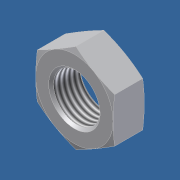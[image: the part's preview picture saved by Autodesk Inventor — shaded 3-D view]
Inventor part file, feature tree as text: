
AUTODESK INVENTOR PART (.ipt)
format: ipt  version: unknown  size: 219,648 bytes
history: native  units: in
note: dims shown in document units (in); Inventor stores cm internally (conversion verified against a paired STEP export)
features: other x70, sketch x3, revolve x2, extrude x1, thread x1
ambient origin geometry x8: Origin, YZ Plane, XZ Plane, XY Plane, X Axis, Y Axis, Z Axis, Center Point
feature tree (77):
  sketch  "Sketch_8"  dims[d0=360.0deg d1=0.38in d2=0.0in]
  sketch  "Sketch_10"  dims[d3=360.0deg d4=0.38in d5=0.0in]
  revolve  "Revolution1"  [1 undecoded]
  extrude  "Extrusion1"  Depth=0.38in TaperAngle=0.0deg
  revolve  "Revolution2"  [1 undecoded]
  thread  "Thread1"  [1 undecoded]
  other  "NUT_XY"
  other  "NUT_YZ"
  other  "NUT_ZX"
  other  "NUT_X"
  other  "NUT_Y"
  other  "NUT_Z"
  other  "NUT_Center"
  other  "a1_XY"
  other  "a1_YZ"
  other  "a1_ZX"
  other  "a1_X"
  other  "a1_Y"
  other  "a1_Z"
  other  "a1_Center"
  other  "a2_XY"
  other  "a2_YZ"
  other  "a2_ZX"
  other  "a2_X"
  other  "a2_Y"
  other  "a2_Z"
  other  "a2_Center"
  other  "b1_XY"
  other  "b1_YZ"
  other  "b1_ZX"
  other  "b1_X"
  other  "b1_Y"
  other  "b1_Z"
  other  "b1_Center"
  other  "b2_XY"
  other  "b2_YZ"
  other  "b2_ZX"
  other  "b2_X"
  other  "b2_Y"
  other  "b2_Z"
  other  "b2_Center"
  other  "e_XY"
  other  "e_YZ"
  other  "e_ZX"
  other  "e_X"
  other  "e_Y"
  other  "e_Z"
  other  "e_Center"
  other  "th1_XY"
  other  "th1_YZ"
  other  "th1_ZX"
  other  "th1_X"
  other  "th1_Y"
  other  "th1_Z"
  other  "th1_Center"
  other  "th2_XY"
  other  "th2_YZ"
  other  "th2_ZX"
  other  "th2_X"
  other  "th2_Y"
  other  "th2_Z"
  other  "th2_Center"
  other  "ol1_XY"
  other  "ol1_YZ"
  other  "ol1_ZX"
  other  "ol1_X"
  other  "ol1_Y"
  other  "ol1_Z"
  other  "ol1_Center"
  other  "ol2_XY"
  other  "ol2_YZ"
  other  "ol2_ZX"
  other  "ol2_X"
  other  "ol2_Y"
  other  "ol2_Z"
  other  "ol2_Center"
  sketch  "Sketch_11"
note: 3 required parameter values undecoded (feature->parameter linkage not recoverable at this tier; creation-order binding heuristic only, values carry confidence <= 0.55)